# Revit family: Rohrschelle Maxima PSM, M16, Ø102-117, Silikon
name_source: partatom
category: HLS-Bauteile
revit_build: Autodesk Revit 2017 (Build: 20190507_1515(x64)
units: mm (PartAtom-declared; Revit-internal decimal feet)

## family parameters
Arbeitsebenenbasiert = Ja
Beim Laden mit Abzugskörper schneiden = Nein
Bemaßung runder Anschluss = Durchmesser verwenden
Gemeinsam genutzt = Ja
Immer vertikal = Nein
Raumberechnungspunkt = Nein
Teiletyp = Normal

## types (3) — shared parameters
A = 29 mm
AB = 4 mm  [stored 0.0131234 ft]
Anschluss = M16
Anschlußhöhe = 29 mm
Bauart = zweiteilig
Baustoffklasse = B2
Brandschutz = 901-1118-000-La-Pk
DF1 = 26 mm
DF2 = 28 mm
DS = 6 mm  [stored 0.019685 ft]
DVS = 15 mm  [stored 0.0492126 ft]
Dämmstärke = 6 mm  [stored 0.019685 ft]
Fabrikat = MEFA
Farbe Schalldämmeinlage = rot
Firma = MEFA Befestigungs- und Montagesysteme GmbH
HGA = 20 mm  [stored 0.0656168 ft]
Kurztext1 = Rohrschelle Maxima PSM 30x3,0
MB = 30 mm  [stored 0.0984252 ft]
MD = 3 mm  [stored 0.00984252 ft]
Material = Stahl
Material Schalldämmeinlage = Silikon
Materialmaße = 30x3,0 mm
Materialname = S235
Mengeneinheit = St
Oberflaeche = galvanisch verzinkt
Schalldämmeinlage = Silikon
Verschluss = Pendelsteckmuttern
Verschluss-Schraube = M8
Vorgabe-Ansicht = 1219 mm
max. zul. Last = 1.70 kN
max. zul. Last horizontal = 0.00 kN
max. zul. Last vertikal = 0.00 kN
vpe = 1 St
zero-valued in all types: Nennweite DN Rohr, Rohraußendurchmesser, Stärke Material

## per-type parameters (varying)
| type | Achsabstand | Artikelnummer | B | Breite | D | D0 | Dmax | Dmin | EAN | Gewicht | Gewicht pro Bauteil | H | Kurztext2 | R | RM | Rohraußendurchmesser Zoll | S | max. Höhe | max. Rohraußendurchmesser | max. Temperaturbeständigkeit | min. Rohraußendurchmesser |
| Maxima PSM, M16, Ø102-106, Silikon | 152 mm | 008464601 | 178 mm | 178 mm | 106 mm | 118 mm | 106 mm | 102 mm | 4250928454973 | 0.50 kg | 0.50 kg | 144 mm | 102 - 106 mm M16 Silikon | 59 mm | 62 mm  [stored 0.203412 ft] | Zoll | 152 mm | 144 mm | 106 mm | 250 °C | 102 mm |
| Maxima PSM, M16, Ø108-112, Silikon | 158 mm | 008465401 | 184 mm  [stored 0.603675 ft] | 184 mm  [stored 0.603675 ft] | 112 mm  [stored 0.367454 ft] | 124 mm  [stored 0.406824 ft] | 112 mm  [stored 0.367454 ft] | 108 mm | 4250928454980 | 0.52 kg | 0.52 kg | 150 mm | 108 - 112 mm M16 Silikon | 62 mm  [stored 0.203412 ft] | 65 mm  [stored 0.213255 ft] | Zoll | 158 mm  [stored 0.518373 ft] | 150 mm | 112 mm  [stored 0.367454 ft] | 250 °C | 108 mm |
| Maxima PSM, M16, Ø113-117, Silikon | 163 mm | 008465901 | 189 mm | 189 mm | 117 mm | 129 mm | 117 mm | 113 mm | 4250928454997 | 0.54 kg | 0.54 kg | 155 mm | 113 - 117 mm M16 Silikon | 65 mm  [stored 0.213255 ft] | 68 mm | 4 Zoll | 163 mm | 155 mm | 117 mm | 246 °C | 113 mm |

note: [stored X ft] marks values corroborated as IEEE doubles in the binary element streams (Revit-internal decimal feet)

## geometry (parser evidence)
native form markers: Sweep x2
no freeform markers — native parametric forms only
